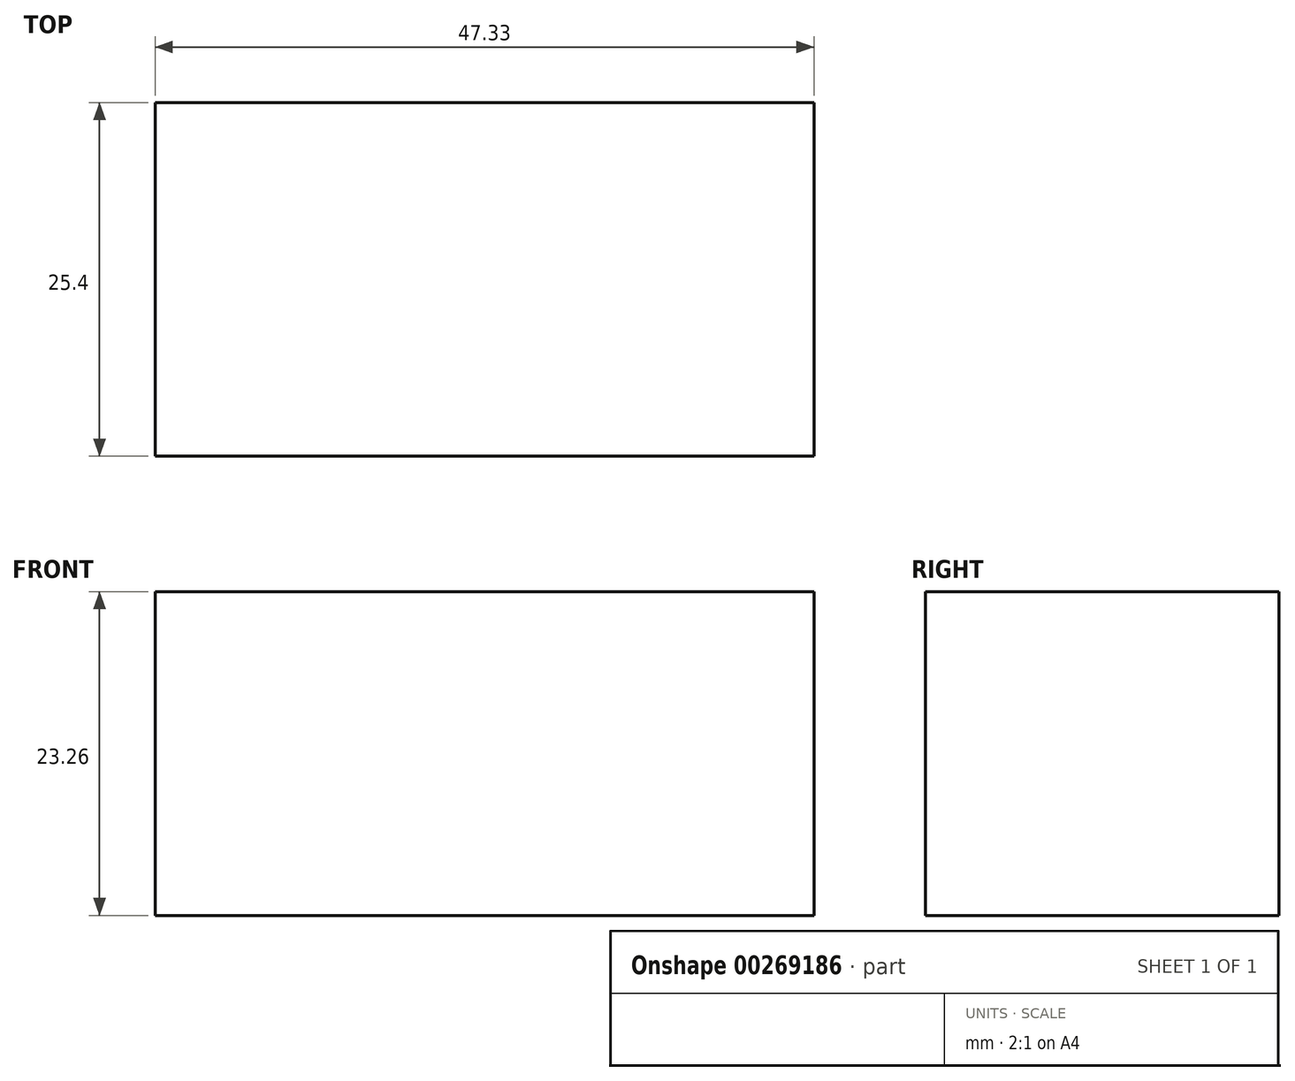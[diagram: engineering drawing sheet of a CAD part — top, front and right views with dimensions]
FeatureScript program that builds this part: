
annotation { "Feature Type Name" : "Feature", "Feature Type Description" : "" }
export const myFeature = defineFeature(function(context is Context, id is Id, definition is map)
    precondition{}
    {
        {
            var Q0;
            Q0=qCreatedBy(makeId("Front.planeOp"),FACE);
            var sketch = newSketch(context, id + "F0", { "sketchPlane" : qUnion([Q0])});
            skLineSegment(sketch, "E0", {"start": v(0, 0) * mm, "end": v(47.33, 0) * mm});
            skLineSegment(sketch, "E1", {"start": v(47.33, 0) * mm, "end": v(47.33, 23.26) * mm});
            skLineSegment(sketch, "E2", {"start": v(47.33, 23.26) * mm, "end": v(0, 23.26) * mm});
            skLineSegment(sketch, "E3", {"start": v(0, 23.26) * mm, "end": v(0, 0) * mm});
            skSolve(sketch);
        }
        {
            var Q0;
            Q0 = qConstructionFilter(qBodyType(qCreatedBy(id + "F0" ,EDGE), BodyType.WIRE), ConstructionObject.NO);
            extrude(context, id + "F1", {"bodyType" : ToolBodyType.SURFACE, "surfaceEntities" : qUnion([Q0]), "depth" : 25.4 * mm});
        }
    });
